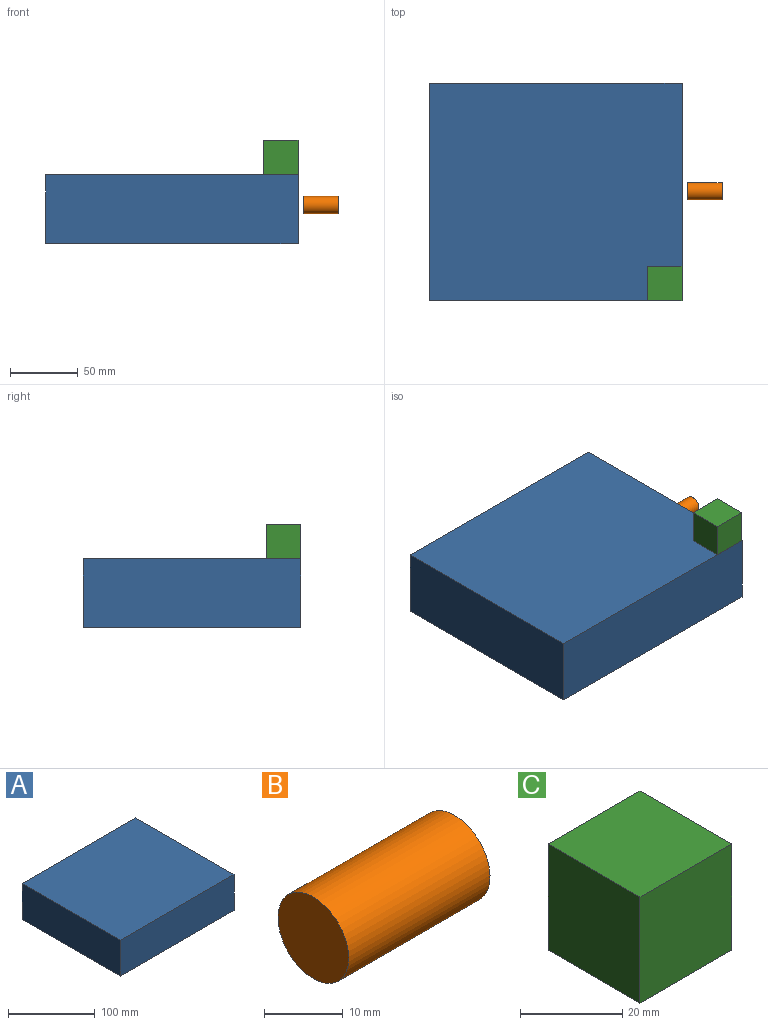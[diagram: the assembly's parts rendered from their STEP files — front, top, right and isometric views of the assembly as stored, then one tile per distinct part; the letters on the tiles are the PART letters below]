
ASSEMBLY  parts=3 mates=2
PART A: 8 faces, bbox 185.9x160.4x50.8 mm
  f0: plane 185.93x50.8mm, normal (0,1,0), area 9445mm2, adj f1,f3,f4,f5
  f1: plane 160.39x50.8mm, normal (-1,0,0), area 8148.1mm2, adj f0,f2,f4,f5
  f2: plane 185.93x50.8mm, normal (0,-1,0), area 9445mm2, adj f1,f3,f4,f5
  f3: plane 160.39x50.8mm, normal (1,0,0), area 7284.5mm2, adj f0,f2,f4,f5,f6
  f4: plane 185.93x160.39mm, normal (0,0,1), area 29821.4mm2, adj f0,f1,f2,f3
  f5: plane 185.93x160.39mm, normal (0,0,-1), area 29821.4mm2, adj f0,f1,f2,f3
  f6: cylinder r=16.58mm len=33.16mm, axis (1,0,0), area 2645.9mm2, adj f3,f7
  f7: plane 33.16x33.16mm, normal (1,0,0), area 863.5mm2, adj f6
PART B: 3 faces, bbox 25.4x12.7x12.7 mm
  f0: cylinder r=6.35mm len=25.4mm, axis (-1,0,0), area 1013.4mm2, adj f1,f2
  f1: plane 12.7x12.7mm, normal (1,0,0), area 126.7mm2, adj f0
  f2: plane 12.7x12.7mm, normal (-1,0,0), area 126.7mm2, adj f0
PART C: 6 faces, bbox 25.4x25.4x25.4 mm
  f0: plane 25.4x25.4mm, normal (0,1,0), area 645.2mm2, adj f1,f3,f4,f5
  f1: plane 25.4x25.4mm, normal (-1,0,0), area 645.2mm2, adj f0,f2,f4,f5
  f2: plane 25.4x25.4mm, normal (0,-1,0), area 645.2mm2, adj f1,f3,f4,f5
  f3: plane 25.4x25.4mm, normal (1,0,0), area 645.2mm2, adj f0,f2,f4,f5
  f4: plane 25.4x25.4mm, normal (0,0,1), area 645.2mm2, adj f0,f1,f2,f3
  f5: plane 25.4x25.4mm, normal (0,0,-1), area 645.2mm2, adj f0,f1,f2,f3
PLACE A t=(-1.7,31,9.96)mm
PLACE B t=(96.37,31,38.46)mm
PLACE C t=(77.98,-34.36,60.76)mm
MATE fastened C.f5 <-> A.f4  axis (0,0,1) through (92.23,-49.83,60.76)mm
MATE slider B.f0 <-> A.f6  axis (-1,0,0) through (96.37,31,38.46)mm
